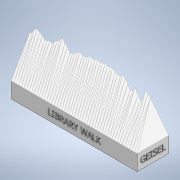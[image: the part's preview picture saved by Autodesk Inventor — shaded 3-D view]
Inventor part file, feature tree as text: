
AUTODESK INVENTOR PART (.ipt)
format: ipt  version: 2020.1 (Build 241239000, 239)  size: 1,894,400 bytes
history: native  units: in
note: dims shown in document units (in); Inventor stores cm internally (conversion verified against a paired STEP export)
features: extrude x5, sketch x5, projected_geometry x4, other x2
ambient origin geometry x8: Origin, YZ Plane, XZ Plane, XY Plane, X Axis, Y Axis, Z Axis, Center Point
bodies: Solid1 (feature_tree)
feature tree (16):
  other  "test"
  extrude  "Extrusion1"  Depth=8.0in
  extrude  "Extrusion2"  Depth=4.9599in
  extrude  "Extrusion3"  Depth=0.1672in
  extrude  "Extrusion4"  Depth=0.2in TaperAngle=0.0deg
  extrude  "Extrusion5"  Depth=0.2in
  sketch  "Sketch1"  dims[d0=1.0in d1=0.0in d2=8.0in]
  sketch  "Sketch2"  dims[d3=1.0in d4=4.9599in]
  projected_geometry  "Projected Loop1"
  sketch  "Sketch3"  dims[d5=0.6656in d6=0.1672in]
  projected_geometry  "Projected Loop2"
  sketch  "Sketch4"  dims[d7=1.52in d8=0.2in d9=0.0in]
  projected_geometry  "Projected Loop3"
  sketch  "Sketch5"  dims[d10=4.0362in d11=1.7927in d12=3.1757in d13=0.9732in d14=8.0in d15=2.0in d16=0.1036in d17=0.5134in d18=0.2627in d19=0.2627in d20=0.2in d21=0.0in d22=1.5193in d23=0.7224in d24=2.0in d25=1.0in d26=0.2404in d27=0.1388in d28=0.2in d29=0.0in d30=8.0in d31=7.0in d32=0.665in d33=0.1675in d34=1.0in d35=0.5in d36=0.2in d37=0.0in]
  projected_geometry  "Projected Loop4"
  other  "MeshFeature1"
